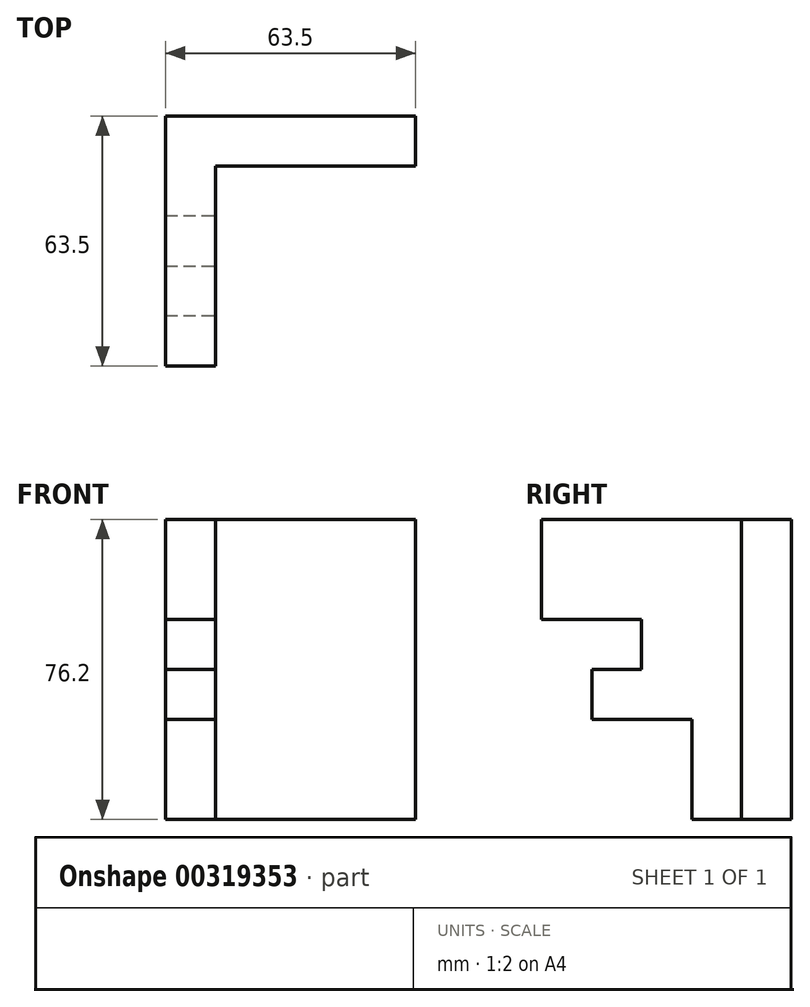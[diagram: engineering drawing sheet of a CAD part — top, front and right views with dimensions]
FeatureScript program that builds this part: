
annotation { "Feature Type Name" : "Feature", "Feature Type Description" : "" }
export const myFeature = defineFeature(function(context is Context, id is Id, definition is map)
    precondition{}
    {
        {
            var Q0;
            Q0=qCreatedBy(makeId("Top.planeOp"),FACE);
            var sketch = newSketch(context, id + "F0", { "sketchPlane" : qUnion([Q0])});
            skLineSegment(sketch, "E0.top", {"start": v(39.47, 33.11) * mm, "end": v(-11.33, 33.11) * mm});
            skLineSegment(sketch, "E0.left", {"start": v(39.47, 45.81) * mm, "end": v(39.47, 33.11) * mm});
            skLineSegment(sketch, "E1.top", {"start": v(-11.33, -17.69) * mm, "end": v(-24.03, -17.69) * mm});
            skLineSegment(sketch, "E1.right", {"start": v(-24.03, 45.81) * mm, "end": v(-24.03, -17.69) * mm});
            skLineSegment(sketch, "E2", {"start": v(-11.33, 33.11) * mm, "end": v(-11.33, -17.69) * mm});
            skLineSegment(sketch, "E3", {"start": v(-24.03, 45.81) * mm, "end": v(39.47, 45.81) * mm});
            skSolve(sketch);
        }
        {
            var Q0;
            Q0=makeQuery(id+"F0.imprint","IMPRINT",FACE,{"disambiguationData":[TD([[makeQuery(id+"F0.imprint","IMPRINT",EDGE,{"derivedFrom":sQuery(id+"F0.wireOp",EDGE,"E0.top")}),-1.0]])]});
            extrude(context, id + "F1", {"entities" : qUnion([Q0]), "depth" : 76.2 * mm});
        }
        {
            var Q0;
            Q0=makeQuery(id+"F1.opExtrude","SWEPT_FACE",FACE,{"disambiguationData":[OSD([sQuery(id+"F0.wireOp",EDGE,"E2")])]});
            var sketch = newSketch(context, id + "F2", { "sketchPlane" : qUnion([Q0])});
            skLineSegment(sketch, "E4", {"start": v(-17.69, 0) * mm, "end": v(20.53, 0) * mm});
            skLineSegment(sketch, "E5", {"start": v(20.53, 0) * mm, "end": v(20.53, 25.4) * mm});
            skLineSegment(sketch, "E6", {"start": v(20.53, 25.4) * mm, "end": v(-4.87, 25.4) * mm});
            skLineSegment(sketch, "E7", {"start": v(-4.87, 25.4) * mm, "end": v(-4.87, 38.1) * mm});
            skLineSegment(sketch, "E8", {"start": v(-4.87, 38.1) * mm, "end": v(7.71, 38.1) * mm});
            skLineSegment(sketch, "E9", {"start": v(7.71, 38.1) * mm, "end": v(7.71, 50.8) * mm});
            skLineSegment(sketch, "E10", {"start": v(7.71, 50.8) * mm, "end": v(-17.69, 50.8) * mm});
            skSolve(sketch);
        }
        {
            var Q0;
            {var subQ0=sQuery(id+"F2.wireOp",EDGE,"E4");Q0=makeQuery(id+"F2.imprint","IMPRINT",FACE,{"disambiguationData":[TD([[makeQuery(id+"F2.imprint","IMPRINT",EDGE,{"derivedFrom":subQ0}),-1.0]])]});}
            extrude(context, id + "F3", {"entities" : qUnion([Q0]), "operationType" : NewBodyOperationType.REMOVE, "oppositeDirection" : true, "depth" : 12.7 * mm});
        }
    });
